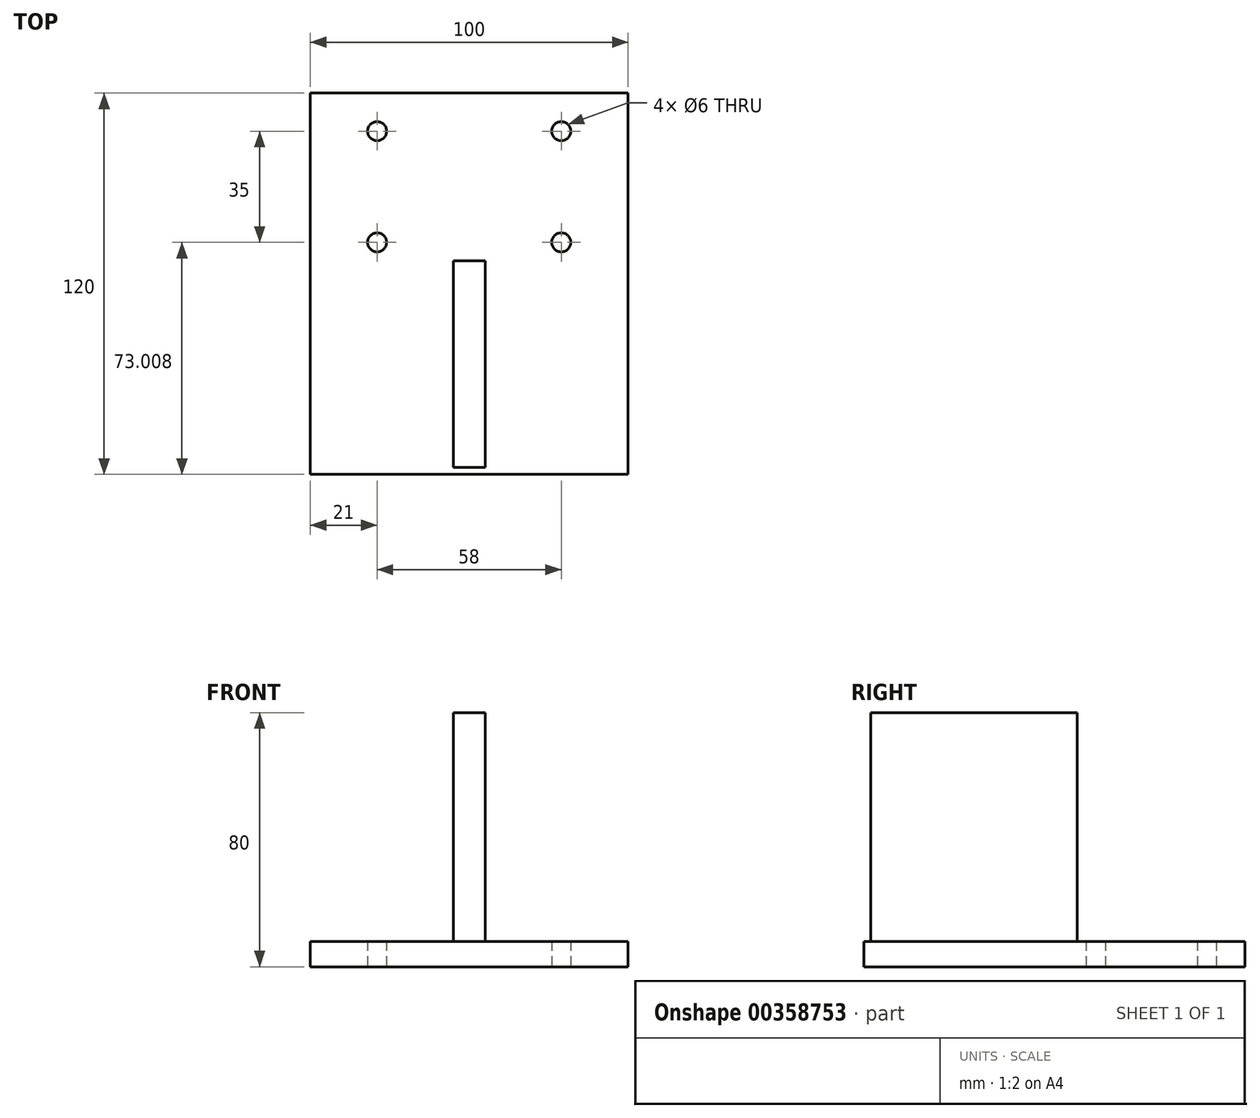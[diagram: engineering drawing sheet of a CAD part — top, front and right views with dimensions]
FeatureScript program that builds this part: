
annotation { "Feature Type Name" : "Feature", "Feature Type Description" : "" }
export const myFeature = defineFeature(function(context is Context, id is Id, definition is map)
    precondition{}
    {
        {
            var Q0;
            Q0=qCreatedBy(makeId("Top.planeOp"),FACE);
            var sketch = newSketch(context, id + "F0", { "sketchPlane" : qUnion([Q0])});
            skLineSegment(sketch, "E0.bottom", {"start": v(-50, 60) * mm, "end": v(50, 60) * mm});
            skLineSegment(sketch, "E0.top", {"start": v(-50, -60) * mm, "end": v(50, -60) * mm});
            skLineSegment(sketch, "E0.left", {"start": v(-50, 60) * mm, "end": v(-50, -60) * mm});
            skLineSegment(sketch, "E0.right", {"start": v(50, 60) * mm, "end": v(50, -60) * mm});
            skCircle(sketch, "E1", {"center": v(-29, 48) * mm, "radius": 3 * mm});
            skCircle(sketch, "E2", {"center": v(29, 48) * mm, "radius": 3 * mm});
            skCircle(sketch, "E3", {"center": v(-29, 13) * mm, "radius": 3 * mm});
            skCircle(sketch, "E4", {"center": v(29, 13) * mm, "radius": 3 * mm});
            skLineSegment(sketch, "E5.bottom", {"start": v(-5, 7.2) * mm, "end": v(5, 7.2) * mm});
            skLineSegment(sketch, "E5.top", {"start": v(-5, -57.8) * mm, "end": v(5, -57.8) * mm});
            skLineSegment(sketch, "E5.left", {"start": v(-5, 7.2) * mm, "end": v(-5, -57.8) * mm});
            skLineSegment(sketch, "E5.right", {"start": v(5, 7.2) * mm, "end": v(5, -57.8) * mm});
            skSolve(sketch);
        }
        {
            var Q0;
            Q0=qSketchRegion(id+"F0",true);
            var Q1;
            Q1=makeQuery(id+"F0.imprint","IMPRINT",FACE,{"disambiguationData":[TD([[makeQuery(id+"F0.imprint","IMPRINT",EDGE,{"derivedFrom":sQuery(id+"F0.wireOp",EDGE,"E5.bottom")}),-1.0]])]});
            extrude(context, id + "F1", {"entities" : qUnion([Q0, Q1]), "depth" : 8 * mm});
        }
        {
            var Q0;
            Q0=makeQuery(id+"F0.imprint","IMPRINT",FACE,{"disambiguationData":[TD([[makeQuery(id+"F0.imprint","IMPRINT",EDGE,{"derivedFrom":sQuery(id+"F0.wireOp",EDGE,"E5.bottom")}),-1.0]])]});
            extrude(context, id + "F2", {"entities" : qUnion([Q0]), "operationType" : NewBodyOperationType.ADD, "depth" : 80 * mm});
        }
    });
